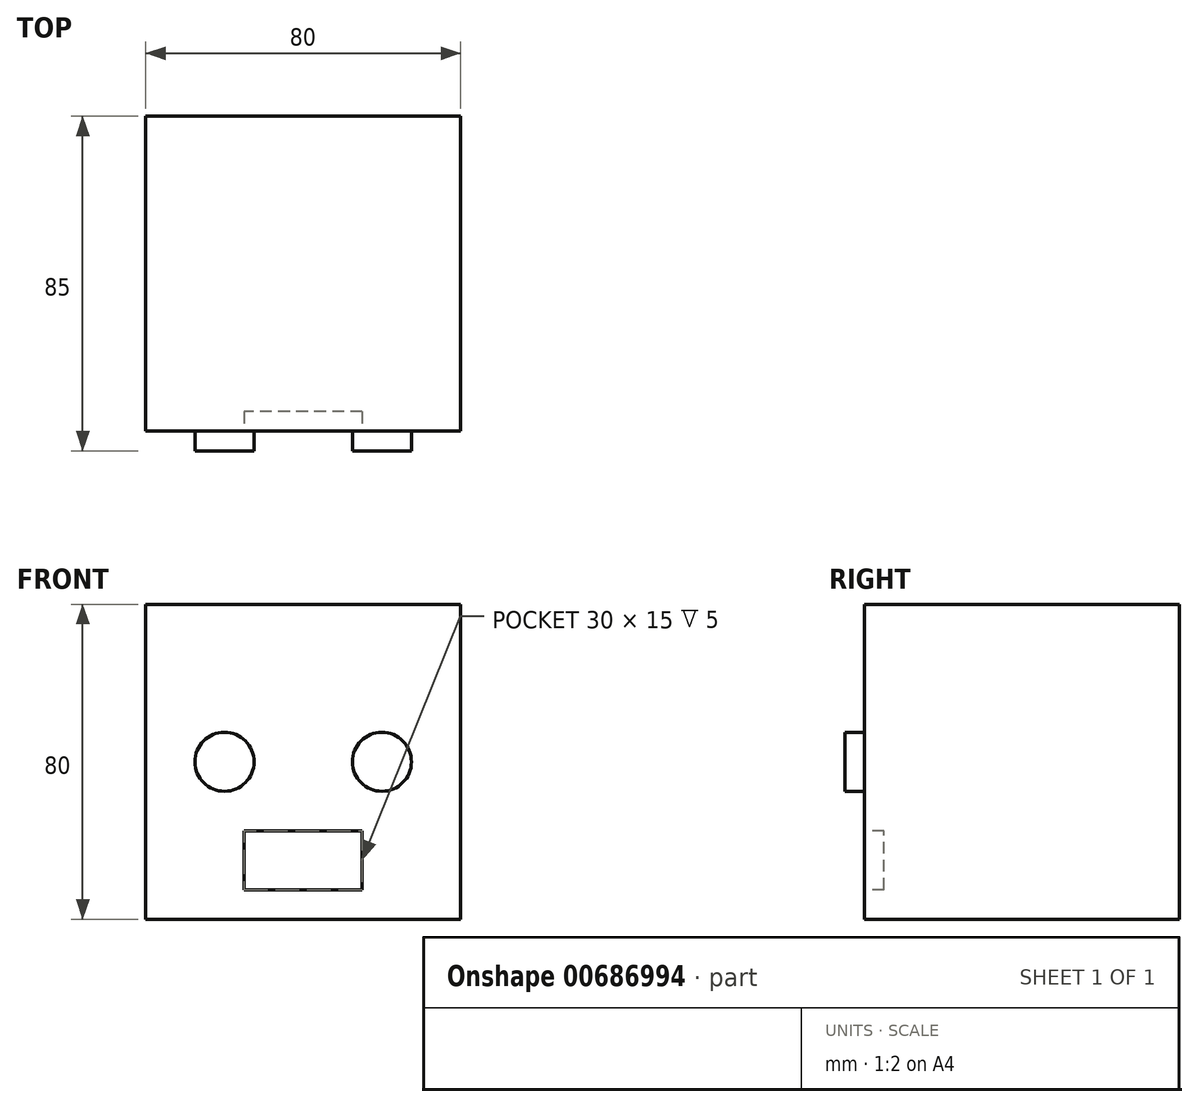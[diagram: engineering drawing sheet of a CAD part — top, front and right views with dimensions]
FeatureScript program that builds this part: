
annotation { "Feature Type Name" : "Feature", "Feature Type Description" : "" }
export const myFeature = defineFeature(function(context is Context, id is Id, definition is map)
    precondition{}
    {
        {
            var Q0;
            Q0=qCreatedBy(makeId("Top.planeOp"),FACE);
            var sketch = newSketch(context, id + "F0", { "sketchPlane" : qUnion([Q0])});
            skLineSegment(sketch, "E0.bottom", {"start": v(40, -40) * mm, "end": v(-40, -40) * mm});
            skLineSegment(sketch, "E0.top", {"start": v(40, 40) * mm, "end": v(-40, 40) * mm});
            skLineSegment(sketch, "E0.left", {"start": v(40, -40) * mm, "end": v(40, 40) * mm});
            skLineSegment(sketch, "E0.right", {"start": v(-40, -40) * mm, "end": v(-40, 40) * mm});
            skPoint(sketch, "E0.middle", {"position": v(0, 0) * mm});
            skSolve(sketch);
        }
        {
            var Q0;
            Q0 = qSketchRegion(id + "F0", true);
            extrude(context, id + "F1", {"entities" : qUnion([Q0]), "depth" : 80 * mm, "offsetDistance" : 25 * mm});
        }
        {
            var Q0;
            Q0=makeQuery(id+"F1.opExtrude","SWEPT_FACE",FACE,{"disambiguationData":[OSD([sQuery(id+"F0.wireOp",EDGE,"E0.bottom")])]});
            var sketch = newSketch(context, id + "F2", { "sketchPlane" : qUnion([Q0])});
            skCircle(sketch, "E1", {"center": v(-20, 40) * mm, "radius": 7.5 * mm});
            skCircle(sketch, "E2", {"center": v(20, 40) * mm, "radius": 7.5 * mm});
            skSolve(sketch);
        }
        {
            var Q0;
            Q0 = qSketchRegion(id + "F2", true);
            extrude(context, id + "F3", {"entities" : qUnion([Q0]), "operationType" : NewBodyOperationType.ADD, "depth" : 5 * mm, "offsetDistance" : 25 * mm});
        }
        {
            var Q0;
            Q0=makeQuery(id+"F1.opExtrude","SWEPT_FACE",FACE,{"disambiguationData":[OSD([sQuery(id+"F0.wireOp",EDGE,"E0.bottom")])]});
            var sketch = newSketch(context, id + "F4", { "sketchPlane" : qUnion([Q0])});
            skLineSegment(sketch, "E3.bottom", {"start": v(15, 7.5) * mm, "end": v(-15, 7.5) * mm});
            skLineSegment(sketch, "E3.top", {"start": v(15, 22.5) * mm, "end": v(-15, 22.5) * mm});
            skLineSegment(sketch, "E3.left", {"start": v(15, 7.5) * mm, "end": v(15, 22.5) * mm});
            skLineSegment(sketch, "E3.right", {"start": v(-15, 7.5) * mm, "end": v(-15, 22.5) * mm});
            skPoint(sketch, "E3.middle", {"position": v(0, 15) * mm});
            skSolve(sketch);
        }
        {
            var Q0;
            Q0 = qSketchRegion(id + "F4", true);
            extrude(context, id + "F5", {"entities" : qUnion([Q0]), "operationType" : NewBodyOperationType.REMOVE, "oppositeDirection" : true, "depth" : 5 * mm, "offsetDistance" : 25 * mm});
        }
    });
